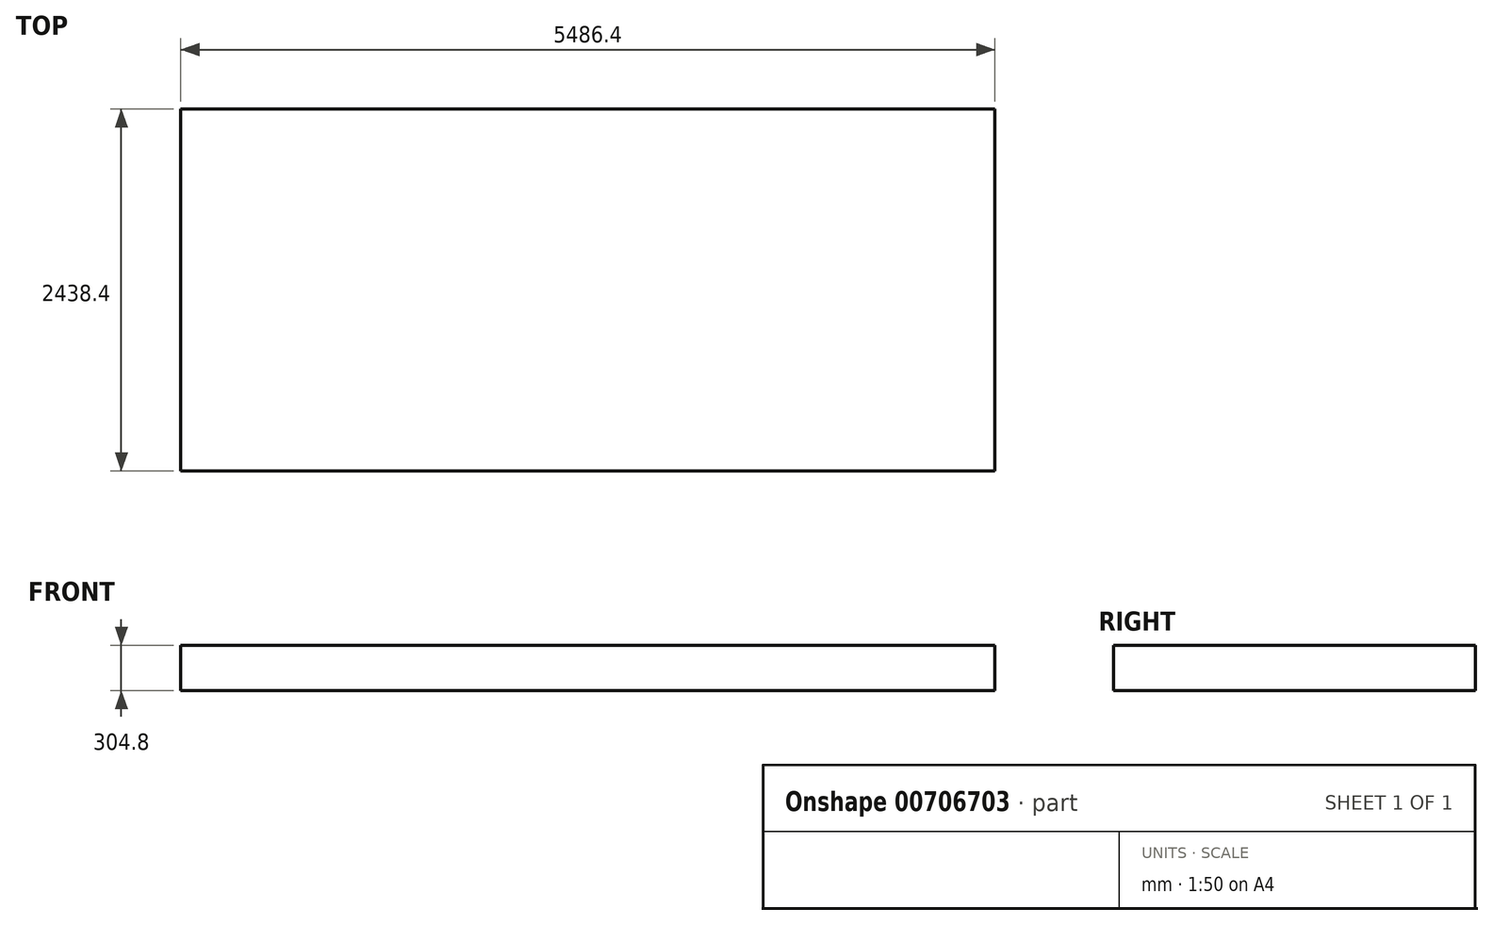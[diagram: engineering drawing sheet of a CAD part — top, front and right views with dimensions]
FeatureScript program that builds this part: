
annotation { "Feature Type Name" : "Feature", "Feature Type Description" : "" }
export const myFeature = defineFeature(function(context is Context, id is Id, definition is map)
    precondition{}
    {
        {
            var Q0;
            Q0=qCreatedBy(makeId("Front.planeOp"),FACE);
            var sketch = newSketch(context, id + "F0", { "sketchPlane" : qUnion([Q0])});
            skLineSegment(sketch, "E0.bottom", {"start": v(0, 0) * mm, "end": v(5486.4, 0) * mm});
            skLineSegment(sketch, "E0.top", {"start": v(0, 304.8) * mm, "end": v(5486.4, 304.8) * mm});
            skLineSegment(sketch, "E0.left", {"start": v(0, 0) * mm, "end": v(0, 304.8) * mm});
            skLineSegment(sketch, "E0.right", {"start": v(5486.4, 0) * mm, "end": v(5486.4, 304.8) * mm});
            skSolve(sketch);
        }
        {
            var Q0;
            Q0=makeQuery(id+"F0.imprint","IMPRINT",FACE,{"disambiguationData":[TD([[makeQuery(id+"F0.imprint","IMPRINT",EDGE,{"derivedFrom":sQuery(id+"F0.wireOp",EDGE,"E0.bottom")}),1.0]])]});
            extrude(context, id + "F1", {"entities" : qUnion([Q0]), "depth" : 2438.4 * mm, "offsetDistance" : 25.4 * mm});
        }
    });
